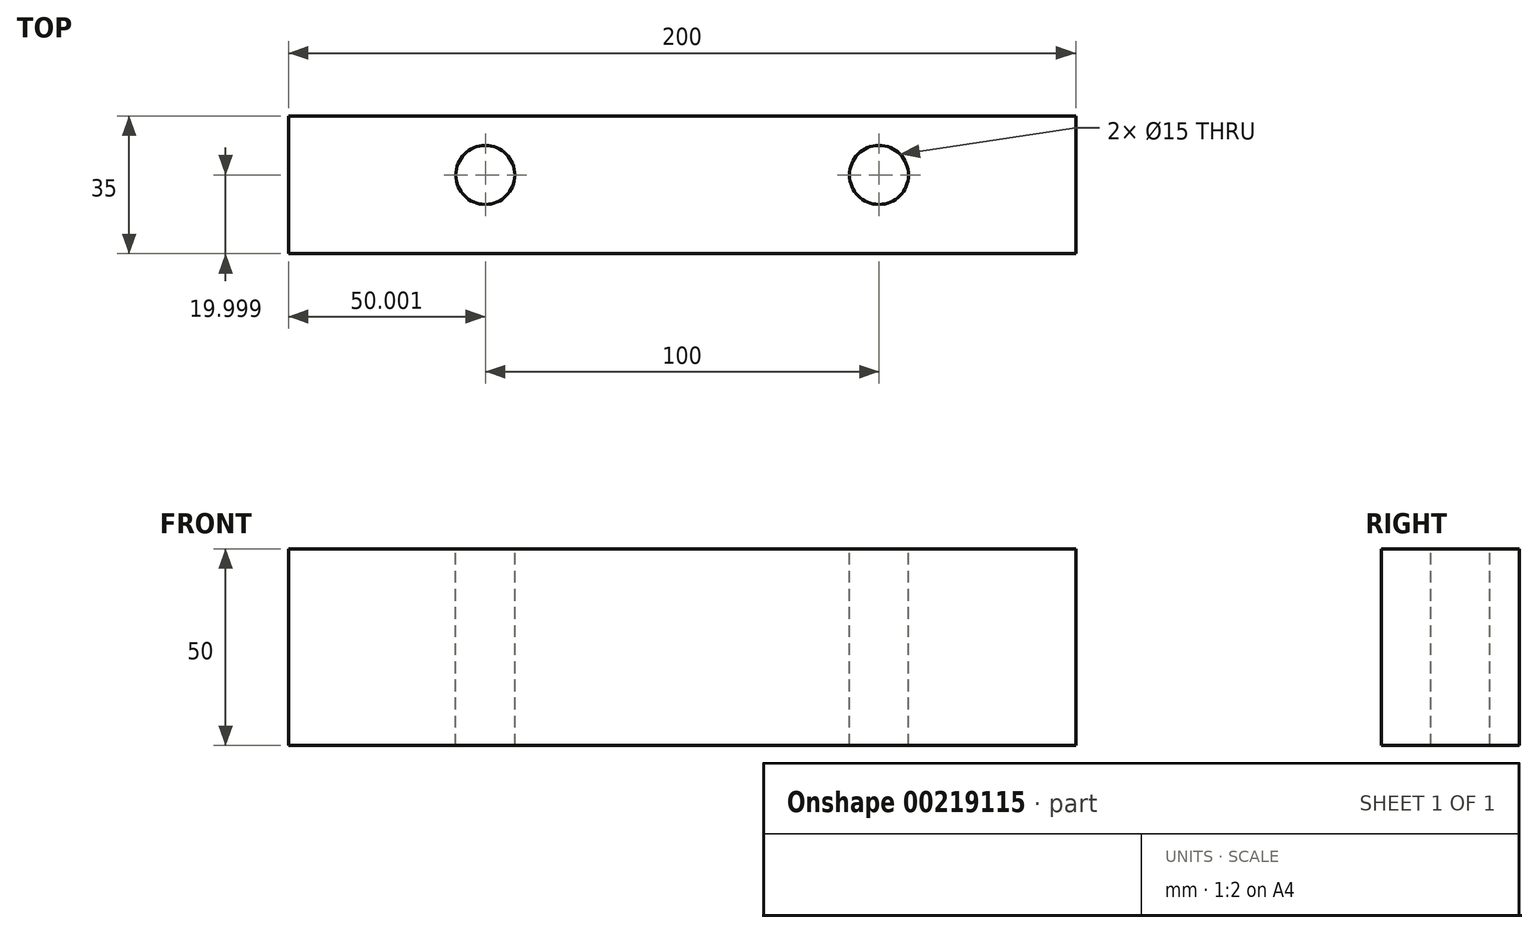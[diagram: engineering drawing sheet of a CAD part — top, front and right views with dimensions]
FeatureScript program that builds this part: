
annotation { "Feature Type Name" : "Feature", "Feature Type Description" : "" }
export const myFeature = defineFeature(function(context is Context, id is Id, definition is map)
    precondition{}
    {
        {
            var Q0;
            Q0=qCreatedBy(makeId("Top.planeOp"),FACE);
            var sketch = newSketch(context, id + "F0", { "sketchPlane" : qUnion([Q0])});
            skLineSegment(sketch, "E0.bottom", {"start": v(-93.52, -7.02) * mm, "end": v(106.48, -7.02) * mm});
            skLineSegment(sketch, "E0.top", {"start": v(-93.52, -42.02) * mm, "end": v(106.48, -42.02) * mm});
            skLineSegment(sketch, "E0.left", {"start": v(-93.52, -7.02) * mm, "end": v(-93.52, -42.02) * mm});
            skLineSegment(sketch, "E0.right", {"start": v(106.48, -7.02) * mm, "end": v(106.48, -42.02) * mm});
            skCircle(sketch, "E1", {"center": v(-43.52, -22.02) * mm, "radius": 7.5 * mm});
            skCircle(sketch, "E2", {"center": v(56.48, -22.02) * mm, "radius": 7.5 * mm});
            skSolve(sketch);
        }
        {
            var Q0;
            Q0=makeQuery(id+"F0.imprint","IMPRINT",FACE,{"disambiguationData":[TD([[makeQuery(id+"F0.imprint","IMPRINT",EDGE,{"derivedFrom":sQuery(id+"F0.wireOp",EDGE,"E0.bottom")}),-1.0]])]});
            extrude(context, id + "F1", {"entities" : qUnion([Q0]), "oppositeDirection" : true, "depth" : 50 * mm});
        }
    });
